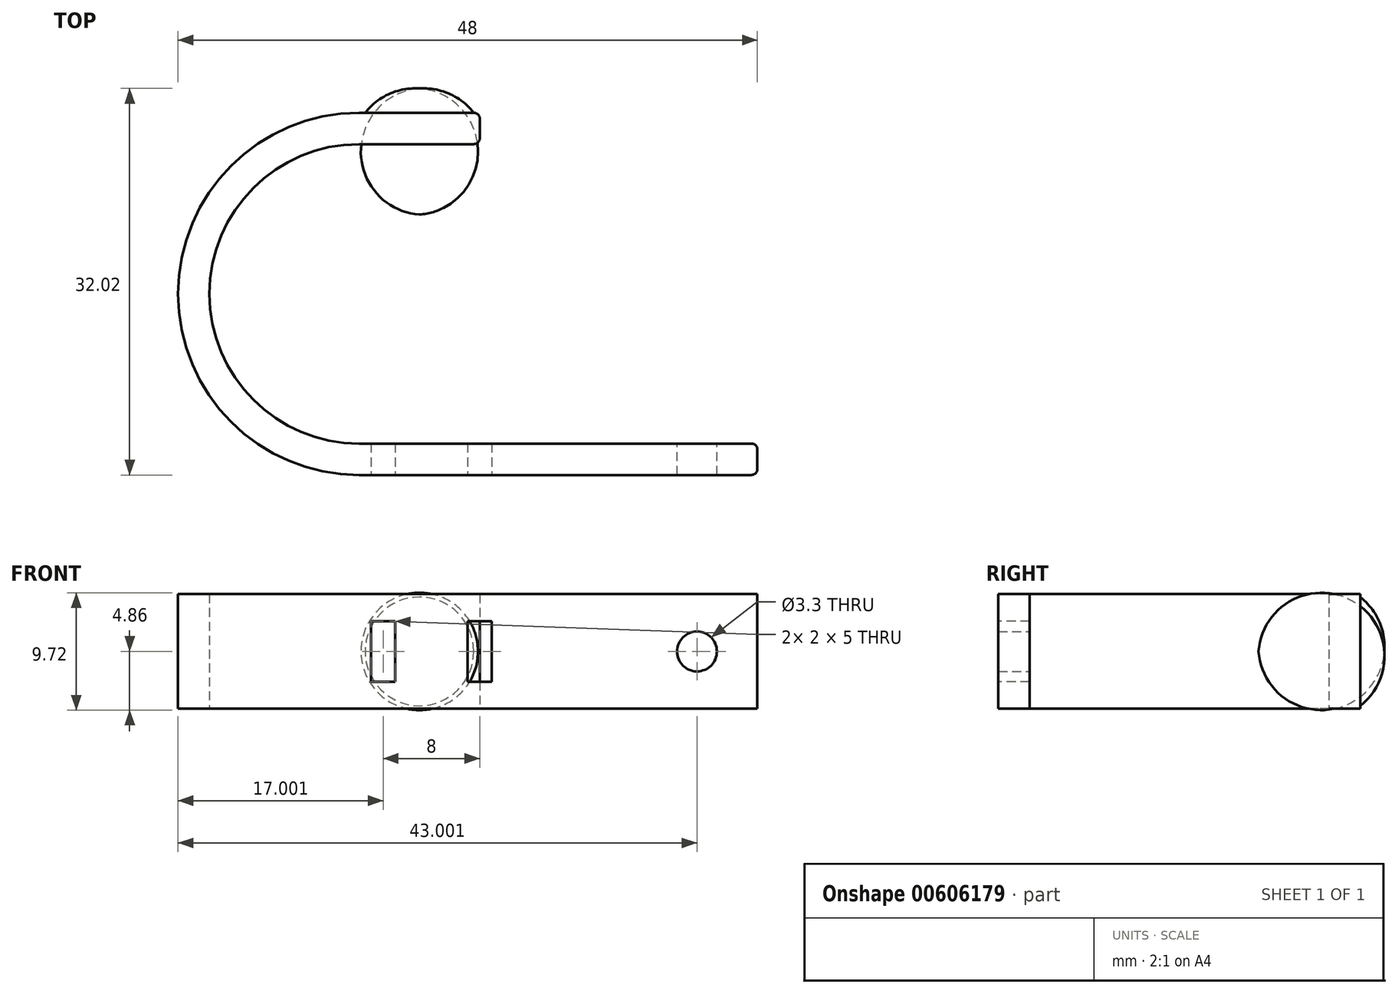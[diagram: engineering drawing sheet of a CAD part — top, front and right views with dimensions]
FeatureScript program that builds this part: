
annotation { "Feature Type Name" : "Feature", "Feature Type Description" : "" }
export const myFeature = defineFeature(function(context is Context, id is Id, definition is map)
    precondition{}
    {
        {
            var Q0;
            Q0=qCreatedBy(makeId("Top.planeOp"),FACE);
            var sketch = newSketch(context, id + "F0", { "sketchPlane" : qUnion([Q0])});
            skLineSegment(sketch, "E0", {"start": v(-13.12, -9.22) * mm, "end": v(19.88, -9.22) * mm});
            skLineSegment(sketch, "E1", {"start": v(19.88, -9.22) * mm, "end": v(19.88, -6.62) * mm});
            skArc(sketch, "E2", {"start": v(-13.12, -9.22) * mm, "mid": v(-28.12, 5.78) * mm, "end": v(-13.12, 20.78) * mm});
            skLineSegment(sketch, "E3", {"start": v(19.88, -6.62) * mm, "end": v(-13.12, -6.62) * mm});
            skArc(sketch, "E4", {"start": v(-13.12, -6.62) * mm, "mid": v(-25.52, 5.78) * mm, "end": v(-13.12, 18.18) * mm});
            skLineSegment(sketch, "E5", {"start": v(-13.12, 20.78) * mm, "end": v(-3.12, 20.78) * mm});
            skLineSegment(sketch, "E6", {"start": v(-3.12, 20.78) * mm, "end": v(-3.12, 18.18) * mm});
            skLineSegment(sketch, "E7", {"start": v(-3.12, 18.18) * mm, "end": v(-13.12, 18.18) * mm});
            skSolve(sketch);
        }
        {
            var Q0;
            Q0 = qSketchRegion(id + "F0", true);
            extrude(context, id + "F1", {"entities" : qUnion([Q0]), "endBound" : BoundingType.SYMMETRIC, "depth" : 9.5 * mm, "offsetDistance" : 25 * mm});
        }
        {
            var Q0;
            Q0=qCreatedBy(makeId("Top.planeOp"),FACE);
            var sketch = newSketch(context, id + "F2", { "sketchPlane" : qUnion([Q0])});
            skLineSegment(sketch, "E8.0", {"start": v(-13.12, 20.78) * mm, "end": v(-3.12, 20.78) * mm});
            skLineSegment(sketch, "E9", {"start": v(-8.12, 20.78) * mm, "end": v(-8.12, 22.78) * mm});
            skArc(sketch, "E10", {"start": v(-3.62, 20.78) * mm, "mid": v(-5.62, 22.35) * mm, "end": v(-8.12, 22.78) * mm});
            skSolve(sketch);
        }
        {
            var Q0;
            {var subQ2=sQuery(id+"F2.wireOp",EDGE,"E9");Q0=makeQuery(id+"F2.imprint","IMPRINT",FACE,{"disambiguationData":[TD([[makeQuery(id+"F2.imprint","IMPRINT",EDGE,{"derivedFrom":subQ2}),-1.0]])]});}
            var Q1;
            Q1 = qConstructionFilter(qBodyType(qCreatedBy(id + "F2" ,EDGE), BodyType.WIRE), ConstructionObject.NO);
            var Q2;
            Q2=sQuery(id+"F2.wireOp",EDGE,"E9");
            revolve(context, id + "F3", {"entities" : qUnion([Q0]), "surfaceEntities" : qUnion([Q1]), "axis" : qUnion([Q2]), "revolveType" : RevolveType.FULL});
        }
        {
            var Q0;
            Q0=makeQuery(id+"F1.opExtrude","SWEPT_FACE",FACE,{"disambiguationData":[OSD([sQuery(id+"F0.wireOp",EDGE,"E3")])]});
            var sketch = newSketch(context, id + "F4", { "sketchPlane" : qUnion([Q0])});
            skPoint(sketch, "E11", {"position": v(-14.88, 0) * mm});
            skPoint(sketch, "E11.positionSnap0", {"position": v(-19.88, 0) * mm});
            skSolve(sketch);
        }
        {
            var Q0;
            Q0=sQuery(id+"F4.wireOp",VERTEX,"E11");
            var Q1;
            Q1=makeQuery(id+"F1.opExtrude","SWEPT_BODY",BODY,{"disambiguationData":[OSD([sQuery(id+"F0.wireOp",EDGE,"E0"),sQuery(id+"F0.wireOp",EDGE,"E1"),sQuery(id+"F0.wireOp",EDGE,"E2"),sQuery(id+"F0.wireOp",EDGE,"E3"),sQuery(id+"F0.wireOp",EDGE,"E4"),sQuery(id+"F0.wireOp",EDGE,"E5"),sQuery(id+"F0.wireOp",EDGE,"E6"),sQuery(id+"F0.wireOp",EDGE,"E7")])]});
            hole(context, id + "F5", {"style" : HoleStyle.SIMPLE, "endStyle" : HoleEndStyle.THROUGH, "standardTappedOrClearance" : lookupTablePath({ "standard" : "ISO", "fit" : "Normal", "size" : "M3", "type" : "Clearance" }), "standardBlindInLast" : lookupTablePath({ "fit" : "Standard", "standard" : "ISO", "size" : "M3", "type" : "Clearance" }), "holeDiameter" : 3.3 * mm, "majorDiameter" : 5 * mm, "isTappedThrough" : true, "tappedDepth" : 12 * mm, "tapClearance" : 3, "locations" : qUnion([Q0]), "scope" : qUnion([Q1])});
        }
        {
            var Q0;
            Q0=makeQuery(id+"F1.opExtrude","SWEPT_EDGE",EDGE,{"disambiguationData":[OSD([sQuery(id+"F0.wireOp",EDGE,"E5"),sQuery(id+"F0.wireOp",EDGE,"E6")])]});
            var Q1;
            Q1=makeQuery(id+"F1.opExtrude","SWEPT_EDGE",EDGE,{"disambiguationData":[OSD([sQuery(id+"F0.wireOp",EDGE,"E6"),sQuery(id+"F0.wireOp",EDGE,"E7")])]});
            var Q2;
            Q2=makeQuery(id+"F1.opExtrude","SWEPT_EDGE",EDGE,{"disambiguationData":[OSD([sQuery(id+"F0.wireOp",EDGE,"E1"),sQuery(id+"F0.wireOp",EDGE,"E3")])]});
            var Q3;
            Q3=makeQuery(id+"F1.opExtrude","SWEPT_EDGE",EDGE,{"disambiguationData":[OSD([sQuery(id+"F0.wireOp",EDGE,"E0"),sQuery(id+"F0.wireOp",EDGE,"E1")])]});
            fillet(context, id + "F6", {"entities" : qUnion([Q0, Q1, Q2, Q3]), "radius" : .5 * mm, "tangentPropagation" : true, "allowEdgeOverflow" : false});
        }
        {
            var Q0;
            Q0=makeQuery(id+"F1.opExtrude","SWEPT_FACE",FACE,{"disambiguationData":[OSD([sQuery(id+"F0.wireOp",EDGE,"E0")])]});
            var sketch = newSketch(context, id + "F7", { "sketchPlane" : qUnion([Q0])});
            skLineSegment(sketch, "E12.bottom", {"start": v(-2.12, 2.5) * mm, "end": v(-4.12, 2.5) * mm});
            skLineSegment(sketch, "E12.top", {"start": v(-2.12, -2.5) * mm, "end": v(-4.12, -2.5) * mm});
            skLineSegment(sketch, "E12.left", {"start": v(-2.12, 2.5) * mm, "end": v(-2.12, -2.5) * mm});
            skLineSegment(sketch, "E12.right", {"start": v(-4.12, 2.5) * mm, "end": v(-4.12, -2.5) * mm});
            skLineSegment(sketch, "E13.bottom", {"start": v(-10.12, 2.5) * mm, "end": v(-12.12, 2.5) * mm});
            skLineSegment(sketch, "E13.top", {"start": v(-10.12, -2.5) * mm, "end": v(-12.12, -2.5) * mm});
            skLineSegment(sketch, "E13.left", {"start": v(-10.12, 2.5) * mm, "end": v(-10.12, -2.5) * mm});
            skLineSegment(sketch, "E13.right", {"start": v(-12.12, 2.5) * mm, "end": v(-12.12, -2.5) * mm});
            skSolve(sketch);
        }
        {
            var Q0;
            Q0 = qSketchRegion(id + "F7", true);
            extrude(context, id + "F8", {"entities" : qUnion([Q0]), "operationType" : NewBodyOperationType.REMOVE, "endBound" : BoundingType.UP_TO_NEXT, "oppositeDirection" : true, "depth" : 25 * mm, "offsetDistance" : 25 * mm});
        }
    });
